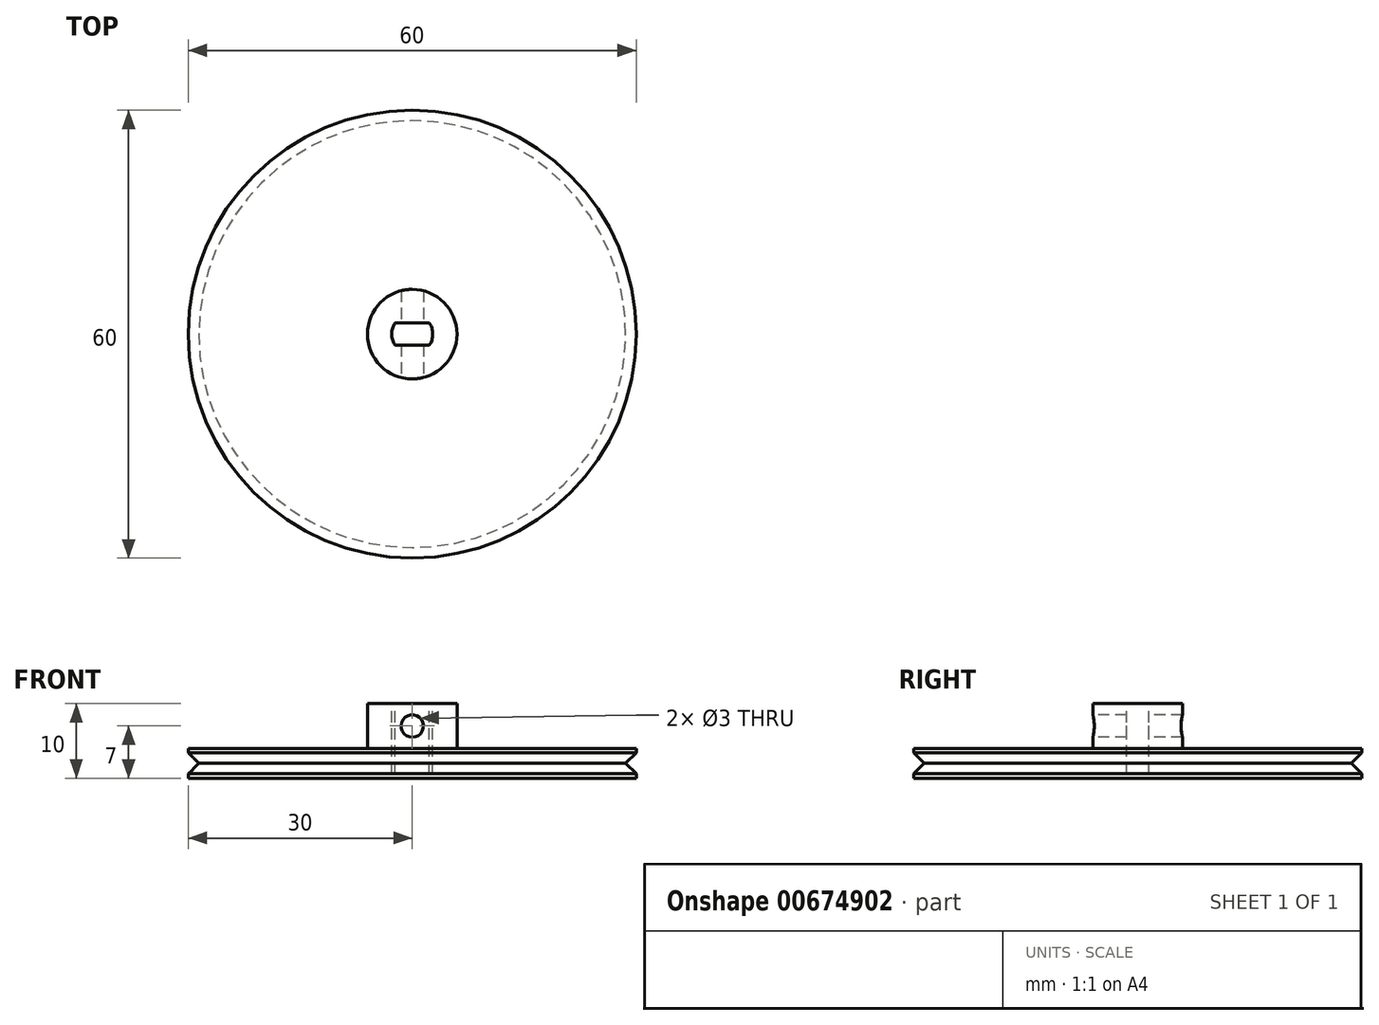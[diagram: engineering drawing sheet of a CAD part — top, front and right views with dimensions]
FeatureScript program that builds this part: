
annotation { "Feature Type Name" : "Feature", "Feature Type Description" : "" }
export const myFeature = defineFeature(function(context is Context, id is Id, definition is map)
    precondition{}
    {
        {
            var Q0;
            Q0=qCreatedBy(makeId("Top.planeOp"),FACE);
            var sketch = newSketch(context, id + "F0", { "sketchPlane" : qUnion([Q0])});
            skCircle(sketch, "E0", {"center": v(0, 0) * mm, "radius": 30 * mm});
            skCircle(sketch, "E1", {"center": v(0, 0) * mm, "radius": 6 * mm});
            skSolve(sketch);
        }
        {
            var Q0;
            Q0=makeQuery(id+"F0.imprint","IMPRINT",FACE,{"disambiguationData":[TD([[makeQuery(id+"F0.imprint","IMPRINT",EDGE,{"derivedFrom":sQuery(id+"F0.wireOp",EDGE,"E1")}),1.0]])]});
            var Q1;
            Q1=makeQuery(id+"F0.imprint","IMPRINT",FACE,{"disambiguationData":[TD([[makeQuery(id+"F0.imprint","IMPRINT",EDGE,{"derivedFrom":sQuery(id+"F0.wireOp",EDGE,"E0")}),1.0]])]});
            extrude(context, id + "F1", {"entities" : qUnion([Q0, Q1]), "oppositeDirection" : true, "depth" : 4 * mm, "offsetDistance" : 25 * mm});
        }
        {
            var Q0;
            Q0=makeQuery(id+"F0.imprint","IMPRINT",FACE,{"disambiguationData":[TD([[makeQuery(id+"F0.imprint","IMPRINT",EDGE,{"derivedFrom":sQuery(id+"F0.wireOp",EDGE,"E1")}),1.0]])]});
            extrude(context, id + "F2", {"entities" : qUnion([Q0]), "operationType" : NewBodyOperationType.ADD, "depth" : 6 * mm, "offsetDistance" : 25 * mm});
        }
        {
            var Q0;
            Q0=qCreatedBy(makeId("Front.planeOp"),FACE);
            var sketch = newSketch(context, id + "F3", { "sketchPlane" : qUnion([Q0])});
            skCircle(sketch, "E2", {"center": v(0, 3) * mm, "radius": 1.5 * mm});
            skSolve(sketch);
        }
        {
            var Q0;
            Q0 = qSketchRegion(id + "F3", true);
            extrude(context, id + "F4", {"entities" : qUnion([Q0]), "operationType" : NewBodyOperationType.REMOVE, "endBound" : BoundingType.SYMMETRIC, "oppositeDirection" : true, "depth" : 25 * mm, "offsetDistance" : 25 * mm});
        }
        {
            var Q0;
            Q0=makeQuery(id+"F2.opExtrude","CAP_FACE",FACE,{"disambiguationData":[OSD([sQuery(id+"F0.wireOp",EDGE,"E1")])],"isStart":false});
            var sketch = newSketch(context, id + "F5", { "sketchPlane" : qUnion([Q0])});
            skLineSegment(sketch, "E3.bottom", {"start": v(-2.3, -1.5) * mm, "end": v(2.3, -1.5) * mm});
            skLineSegment(sketch, "E3.top", {"start": v(-2.3, 1.5) * mm, "end": v(2.3, 1.5) * mm});
            skLineSegment(sketch, "E3.left", {"start": v(-2.3, -1.5) * mm, "end": v(-2.3, 1.5) * mm});
            skLineSegment(sketch, "E3.right", {"start": v(2.3, -1.5) * mm, "end": v(2.3, 1.5) * mm});
            skPoint(sketch, "E3.middle", {"position": v(0, 0) * mm});
            skArc(sketch, "E4", {"start": v(-2.3, 1.5) * mm, "mid": v(-2.75, 0) * mm, "end": v(-2.3, -1.5) * mm});
            skArc(sketch, "E5", {"start": v(2.3, -1.5) * mm, "mid": v(2.75, 0) * mm, "end": v(2.3, 1.5) * mm});
            skSolve(sketch);
        }
        {
            var Q0;
            Q0 = qSketchRegion(id + "F5", true);
            extrude(context, id + "F6", {"entities" : qUnion([Q0]), "operationType" : NewBodyOperationType.REMOVE, "oppositeDirection" : true, "depth" : 9.4 * mm, "offsetDistance" : 25 * mm});
        }
        {
            var Q0;
            Q0=qCreatedBy(makeId("Front.planeOp"),FACE);
            var sketch = newSketch(context, id + "F7", { "sketchPlane" : qUnion([Q0])});
            skLineSegment(sketch, "E6", {"start": v(30, 0) * mm, "end": v(30, -4) * mm, "construction": true});
            skLineSegment(sketch, "E7", {"start": v(30, -0.59) * mm, "end": v(28.59, -2) * mm});
            skLineSegment(sketch, "E8", {"start": v(28.59, -2) * mm, "end": v(30, -3.41) * mm});
            skLineSegment(sketch, "E9", {"start": v(30, -2) * mm, "end": v(25.84, -2) * mm, "construction": true});
            skLineSegment(sketch, "E10", {"start": v(0, 13.1) * mm, "end": v(0, -11.57) * mm, "construction": true});
            skLineSegment(sketch, "E11", {"start": v(30, -0.59) * mm, "end": v(30, -3.41) * mm});
            skSolve(sketch);
        }
        {
            var Q0;
            Q0 = qSketchRegion(id + "F7", true);
            var Q1;
            Q1 = qConstructionFilter(qBodyType(qCreatedBy(id + "F7" ,EDGE), BodyType.WIRE), ConstructionObject.NO);
            var Q2;
            Q2=sQuery(id+"F7.wireOp",EDGE,"E10");
            revolve(context, id + "F8", {"operationType" : NewBodyOperationType.REMOVE, "entities" : qUnion([Q0]), "surfaceEntities" : qUnion([Q1]), "axis" : qUnion([Q2]), "revolveType" : RevolveType.FULL, "oppositeDirection" : true});
        }
    });
